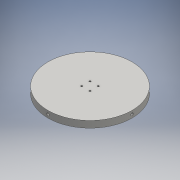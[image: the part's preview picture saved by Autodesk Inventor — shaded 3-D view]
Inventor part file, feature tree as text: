
AUTODESK INVENTOR PART (.ipt)
format: ipt  version: 2016 (Build 200138000, 138)  size: 141,312 bytes
history: native  units: mm
features: thread x8, extrude x6, sketch x6, other x5
ambient origin geometry x8: Origin, YZ Plane, XZ Plane, XY Plane, X Axis, Y Axis, Z Axis, Center Point
bodies: Body1 (feature_tree)
feature tree (25):
  other  "ソリッド1"
  extrude  "押し出し1"  Depth=101.0mm
  extrude  "押し出し2"  Depth=8.0mm TaperAngle=0.0deg
  other  "作業平面1"
  other  "作業平面2"
  other  "作業平面3"
  other  "作業平面4"
  extrude  "押し出し3"  Depth=10.0mm
  extrude  "押し出し4"  Depth=10.0mm
  extrude  "押し出し5"  Depth=2.0mm
  extrude  "押し出し6"  Depth=2.0mm
  thread  "ねじ1"
  thread  "ねじ2"
  thread  "ねじ3"
  thread  "ねじ4"
  thread  "ねじ5"
  thread  "ねじ6"
  thread  "ねじ7"
  thread  "ねじ8"
  sketch  "スケッチ1"
  sketch  "スケッチ2"
  sketch  "スケッチ3"
  sketch  "スケッチ4"
  sketch  "スケッチ5"
  sketch  "スケッチ6"
